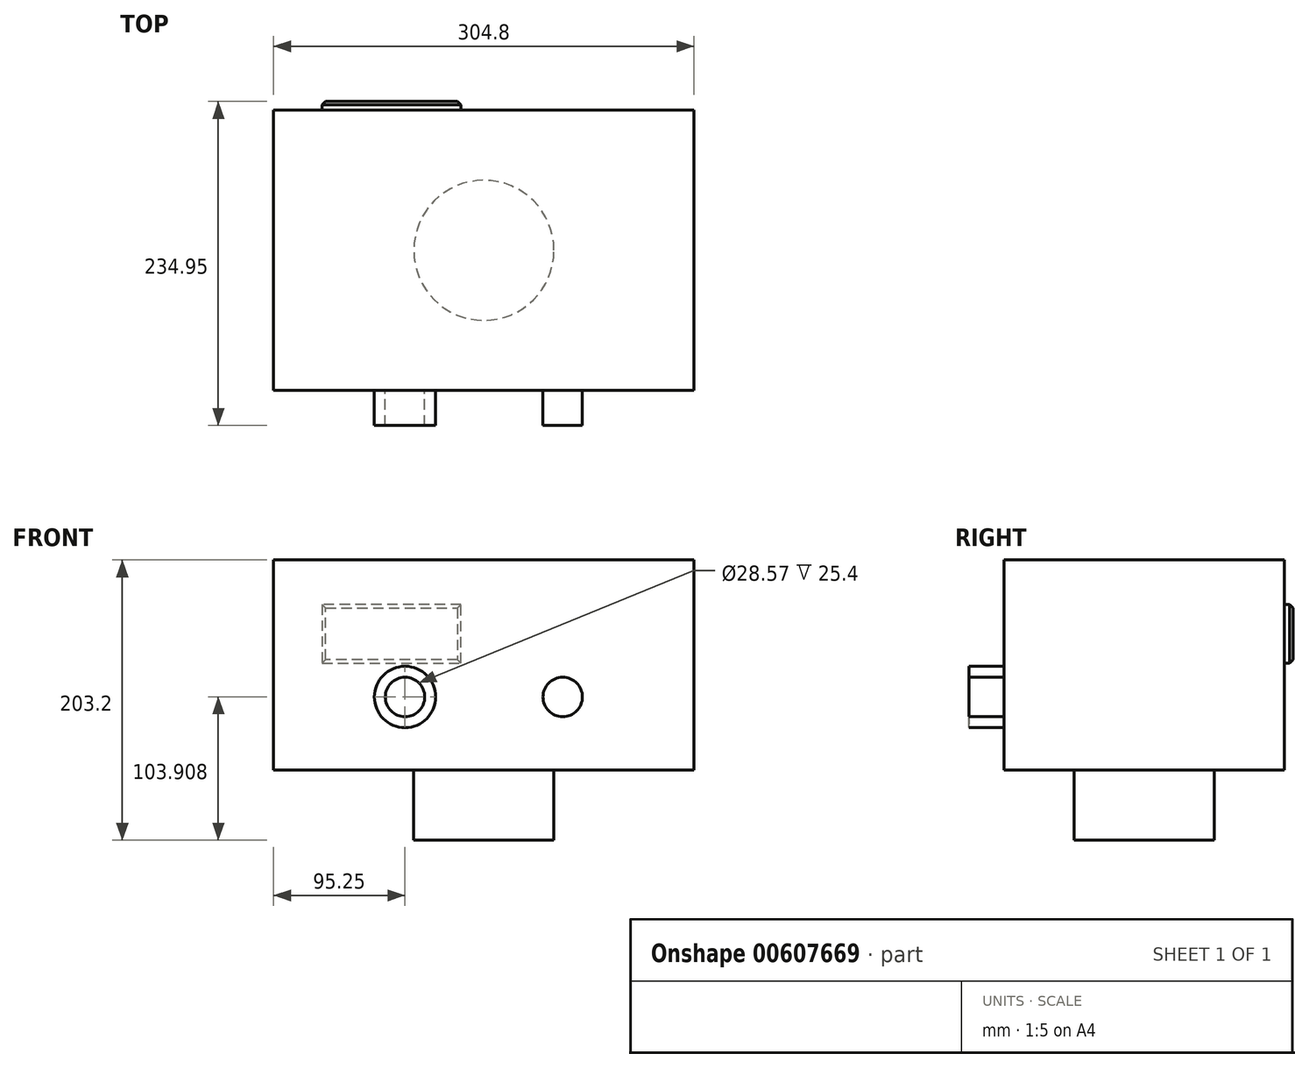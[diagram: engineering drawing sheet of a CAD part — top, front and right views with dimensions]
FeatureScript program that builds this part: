
annotation { "Feature Type Name" : "Feature", "Feature Type Description" : "" }
export const myFeature = defineFeature(function(context is Context, id is Id, definition is map)
    precondition{}
    {
        {
            var Q0;
            Q0=qCreatedBy(makeId("Top.planeOp"),FACE);
            var sketch = newSketch(context, id + "F0", { "sketchPlane" : qUnion([Q0])});
            skLineSegment(sketch, "E0", {"start": v(0, 0) * mm, "end": v(152.4, 0) * mm});
            skLineSegment(sketch, "E1", {"start": v(0, 0) * mm, "end": v(0, 101.6) * mm});
            skLineSegment(sketch, "E2", {"start": v(0, 0) * mm, "end": v(0, -101.6) * mm});
            skLineSegment(sketch, "E3", {"start": v(0, 101.6) * mm, "end": v(152.4, 101.6) * mm});
            skLineSegment(sketch, "E4", {"start": v(0, 0) * mm, "end": v(36.33, -35.5) * mm});
            skCircle(sketch, "E5", {"center": v(0, 0) * mm, "radius": 50.8 * mm});
            skLineSegment(sketch, "E6.bottom", {"start": v(152.4, 101.6) * mm, "end": v(-152.4, 101.6) * mm});
            skLineSegment(sketch, "E6.top", {"start": v(152.4, -101.6) * mm, "end": v(-152.4, -101.6) * mm});
            skLineSegment(sketch, "E6.left", {"start": v(152.4, 101.6) * mm, "end": v(152.4, -101.6) * mm});
            skLineSegment(sketch, "E6.right", {"start": v(-152.4, 101.6) * mm, "end": v(-152.4, -101.6) * mm});
            skSolve(sketch);
        }
        {
            var Q0;
            {var subQ4=sQuery(id+"F0.wireOp",EDGE,"E0");var subQ8=sQuery(id+"F0.wireOp",EDGE,"E6.left");var subQ9=makeQuery(id+"F0.imprint","INTERSECT",VERTEX,{"derivedFrom":[subQ4,subQ8]});Q0=makeQuery(id+"F0.imprint","IMPRINT",FACE,{"disambiguationData":[TD([[makeQuery(id+"F0.imprint","IMPRINT",EDGE,{"disambiguationData":[TD([[subQ9,1.0]])],"derivedFrom":subQ4}),-1.0]])]});}
            var Q1;
            {var subQ1=sQuery(id+"F0.wireOp",EDGE,"E0");var subQ7=sQuery(id+"F0.wireOp",EDGE,"E6.left");var subQ9=makeQuery(id+"F0.imprint","INTERSECT",VERTEX,{"derivedFrom":[subQ1,subQ7]});Q1=makeQuery(id+"F0.imprint","IMPRINT",FACE,{"disambiguationData":[TD([[makeQuery(id+"F0.imprint","IMPRINT",EDGE,{"disambiguationData":[TD([[subQ9,1.0]])],"derivedFrom":subQ1}),1.0]])]});}
            var Q2;
            {var subQ3=sQuery(id+"F0.wireOp",EDGE,"E6.right");Q2=makeQuery(id+"F0.imprint","IMPRINT",FACE,{"disambiguationData":[TD([[makeQuery(id+"F0.imprint","IMPRINT",EDGE,{"derivedFrom":subQ3}),1.0]])]});}
            var Q3;
            {var subQ1=sQuery(id+"F0.wireOp",EDGE,"E1");var subQ3=sQuery(id+"F0.wireOp",EDGE,"E5");var subQ4=makeQuery(id+"F0.imprint","INTERSECT",VERTEX,{"derivedFrom":[subQ1,subQ3]});Q3=makeQuery(id+"F0.imprint","IMPRINT",FACE,{"disambiguationData":[TD([[makeQuery(id+"F0.imprint","IMPRINT",EDGE,{"disambiguationData":[TD([[subQ4,-1.0]])],"derivedFrom":subQ3}),1.0]])]});}
            var Q4;
            {var subQ1=sQuery(id+"F0.wireOp",EDGE,"E0");var subQ3=sQuery(id+"F0.wireOp",EDGE,"E5");var subQ4=makeQuery(id+"F0.imprint","INTERSECT",VERTEX,{"derivedFrom":[subQ1,subQ3]});Q4=makeQuery(id+"F0.imprint","IMPRINT",FACE,{"disambiguationData":[TD([[makeQuery(id+"F0.imprint","IMPRINT",EDGE,{"disambiguationData":[TD([[subQ4,-1.0]])],"derivedFrom":subQ3}),1.0]])]});}
            var Q5;
            {var subQ0=sQuery(id+"F0.wireOp",EDGE,"E4");Q5=makeQuery(id+"F0.imprint","IMPRINT",FACE,{"disambiguationData":[TD([[makeQuery(id+"F0.imprint","IMPRINT",EDGE,{"derivedFrom":subQ0}),-1.0]])]});}
            var Q6;
            {var subQ0=sQuery(id+"F0.wireOp",EDGE,"E4");Q6=makeQuery(id+"F0.imprint","IMPRINT",FACE,{"disambiguationData":[TD([[makeQuery(id+"F0.imprint","IMPRINT",EDGE,{"derivedFrom":subQ0}),1.0]])]});}
            extrude(context, id + "F1", {"entities" : qUnion([Q0, Q1, Q2, Q3, Q4, Q5, Q6]), "depth" : 152.4 * mm, "offsetDistance" : 25.4 * mm});
        }
        {
            var Q0;
            {var subQ0=sQuery(id+"F0.wireOp",EDGE,"E4");Q0=makeQuery(id+"F0.imprint","IMPRINT",FACE,{"disambiguationData":[TD([[makeQuery(id+"F0.imprint","IMPRINT",EDGE,{"derivedFrom":subQ0}),-1.0]])]});}
            var Q1;
            {var subQ0=sQuery(id+"F0.wireOp",EDGE,"E4");Q1=makeQuery(id+"F0.imprint","IMPRINT",FACE,{"disambiguationData":[TD([[makeQuery(id+"F0.imprint","IMPRINT",EDGE,{"derivedFrom":subQ0}),1.0]])]});}
            var Q2;
            {var subQ1=sQuery(id+"F0.wireOp",EDGE,"E0");var subQ3=sQuery(id+"F0.wireOp",EDGE,"E5");var subQ4=makeQuery(id+"F0.imprint","INTERSECT",VERTEX,{"derivedFrom":[subQ1,subQ3]});Q2=makeQuery(id+"F0.imprint","IMPRINT",FACE,{"disambiguationData":[TD([[makeQuery(id+"F0.imprint","IMPRINT",EDGE,{"disambiguationData":[TD([[subQ4,-1.0]])],"derivedFrom":subQ3}),1.0]])]});}
            var Q3;
            {var subQ1=sQuery(id+"F0.wireOp",EDGE,"E1");var subQ3=sQuery(id+"F0.wireOp",EDGE,"E5");var subQ4=makeQuery(id+"F0.imprint","INTERSECT",VERTEX,{"derivedFrom":[subQ1,subQ3]});Q3=makeQuery(id+"F0.imprint","IMPRINT",FACE,{"disambiguationData":[TD([[makeQuery(id+"F0.imprint","IMPRINT",EDGE,{"disambiguationData":[TD([[subQ4,-1.0]])],"derivedFrom":subQ3}),1.0]])]});}
            extrude(context, id + "F2", {"entities" : qUnion([Q0, Q1, Q2, Q3]), "operationType" : NewBodyOperationType.ADD, "oppositeDirection" : true, "depth" : 50.8 * mm, "offsetDistance" : 25.4 * mm});
        }
        {
            var Q0;
            Q0=makeQuery(id+"F1.opExtrude","SWEPT_FACE",FACE,{"disambiguationData":[OSD([sQuery(id+"F0.wireOp",EDGE,"E6.top")])]});
            var sketch = newSketch(context, id + "F3", { "sketchPlane" : qUnion([Q0])});
            skLineSegment(sketch, "E7", {"start": v(152.4, 0) * mm, "end": v(152.4, 53.1) * mm});
            skLineSegment(sketch, "E8", {"start": v(152.4, 53.1) * mm, "end": v(-152.4, 53.1) * mm});
            skLineSegment(sketch, "E9", {"start": v(-152.4, 53.1) * mm, "end": v(-57.15, 53.1) * mm});
            skLineSegment(sketch, "E10", {"start": v(152.4, 53.1) * mm, "end": v(57.15, 53.1) * mm});
            skCircle(sketch, "E11", {"center": v(-57.15, 53.1) * mm, "radius": 22.23 * mm});
            skCircle(sketch, "E12", {"center": v(57.15, 53.1) * mm, "radius": 22.23 * mm});
            skCircle(sketch, "E13", {"center": v(-57.15, 53.1) * mm, "radius": 14.29 * mm});
            skCircle(sketch, "E14", {"center": v(57.15, 53.1) * mm, "radius": 14.29 * mm});
            skSolve(sketch);
        }
        {
            var Q0;
            {var subQ0=sQuery(id+"F3.wireOp",EDGE,"E14");var subQ1=sQuery(id+"F3.wireOp",EDGE,"E8");var subQ2=makeQuery(id+"F3.imprint","INTERSECT",VERTEX,{"derivedFrom":[subQ1,subQ0]});Q0=makeQuery(id+"F3.imprint","IMPRINT",FACE,{"disambiguationData":[TD([[makeQuery(id+"F3.imprint","IMPRINT",EDGE,{"disambiguationData":[TD([[subQ2,-1.0]])],"derivedFrom":subQ1}),-1.0]])]});}
            var Q1;
            {var subQ0=sQuery(id+"F3.wireOp",EDGE,"E14");var subQ1=sQuery(id+"F3.wireOp",EDGE,"E8");var subQ2=makeQuery(id+"F3.imprint","INTERSECT",VERTEX,{"derivedFrom":[subQ1,subQ0]});Q1=makeQuery(id+"F3.imprint","IMPRINT",FACE,{"disambiguationData":[TD([[makeQuery(id+"F3.imprint","IMPRINT",EDGE,{"disambiguationData":[TD([[subQ2,-1.0]])],"derivedFrom":subQ1}),1.0]])]});}
            var Q2;
            {var subQ0=sQuery(id+"F3.wireOp",EDGE,"E11");var subQ1=sQuery(id+"F3.wireOp",EDGE,"E8");var subQ2=makeQuery(id+"F3.imprint","INTERSECT",VERTEX,{"derivedFrom":[subQ1,subQ0]});Q2=makeQuery(id+"F3.imprint","IMPRINT",FACE,{"disambiguationData":[TD([[makeQuery(id+"F3.imprint","IMPRINT",EDGE,{"disambiguationData":[TD([[subQ2,-1.0]])],"derivedFrom":subQ1}),-1.0]])]});}
            var Q3;
            {var subQ0=sQuery(id+"F3.wireOp",EDGE,"E11");var subQ1=sQuery(id+"F3.wireOp",EDGE,"E8");var subQ2=makeQuery(id+"F3.imprint","INTERSECT",VERTEX,{"derivedFrom":[subQ1,subQ0]});Q3=makeQuery(id+"F3.imprint","IMPRINT",FACE,{"disambiguationData":[TD([[makeQuery(id+"F3.imprint","IMPRINT",EDGE,{"disambiguationData":[TD([[subQ2,-1.0]])],"derivedFrom":subQ1}),1.0]])]});}
            var Q4;
            Q4=sQuery(id+"F3.wireOp",EDGE,"E12");
            var Q5;
            Q5=sQuery(id+"F3.wireOp",EDGE,"E14");
            var Q6;
            Q6=sQuery(id+"F3.wireOp",EDGE,"E11");
            var Q7;
            Q7=sQuery(id+"F3.wireOp",EDGE,"E13");
            extrude(context, id + "F4", {"entities" : qUnion([Q0, Q1, Q2, Q3]), "operationType" : NewBodyOperationType.ADD, "surfaceEntities" : qUnion([Q4, Q5, Q6, Q7]), "depth" : 25.4 * mm, "offsetDistance" : 25.4 * mm});
        }
        {
            var Q0;
            Q0=makeQuery(id+"F1.opExtrude","SWEPT_FACE",FACE,{"disambiguationData":[OSD([sQuery(id+"F0.wireOp",EDGE,"E6.bottom")])]});
            var sketch = newSketch(context, id + "F5", { "sketchPlane" : qUnion([Q0])});
            skLineSegment(sketch, "E15.bottom", {"start": v(16.6, 77.64) * mm, "end": v(117.3, 77.64) * mm});
            skLineSegment(sketch, "E15.top", {"start": v(16.6, 120) * mm, "end": v(117.3, 120) * mm});
            skLineSegment(sketch, "E15.left", {"start": v(16.6, 77.64) * mm, "end": v(16.6, 120) * mm});
            skLineSegment(sketch, "E15.right", {"start": v(117.3, 77.64) * mm, "end": v(117.3, 120) * mm});
            skSolve(sketch);
        }
        {
            var Q0;
            Q0=makeQuery(id+"F5.imprint","IMPRINT",FACE,{"disambiguationData":[TD([[makeQuery(id+"F5.imprint","IMPRINT",EDGE,{"derivedFrom":sQuery(id+"F5.wireOp",EDGE,"E15.bottom")}),1.0]])]});
            extrude(context, id + "F6", {"entities" : qUnion([Q0]), "depth" : 6.35 * mm, "offsetDistance" : 25.4 * mm});
        }
        {
            var Q0;
            Q0=makeQuery(id+"F6.opExtrude","CAP_EDGE",EDGE,{"disambiguationData":[OSD([sQuery(id+"F5.wireOp",EDGE,"E15.top")])],"isStart":false});
            var Q1;
            Q1=makeQuery(id+"F6.opExtrude","CAP_EDGE",EDGE,{"disambiguationData":[OSD([sQuery(id+"F5.wireOp",EDGE,"E15.right")])],"isStart":false});
            var Q2;
            Q2=makeQuery(id+"F6.opExtrude","CAP_EDGE",EDGE,{"disambiguationData":[OSD([sQuery(id+"F5.wireOp",EDGE,"E15.left")])],"isStart":false});
            var Q3;
            Q3=makeQuery(id+"F6.opExtrude","CAP_EDGE",EDGE,{"disambiguationData":[OSD([sQuery(id+"F5.wireOp",EDGE,"E15.bottom")])],"isStart":false});
            chamfer(context, id + "F7", {"entities" : qUnion([Q0, Q1, Q2, Q3]), "width" : 2.54 * mm, "tangentPropagation" : true});
        }
    });
